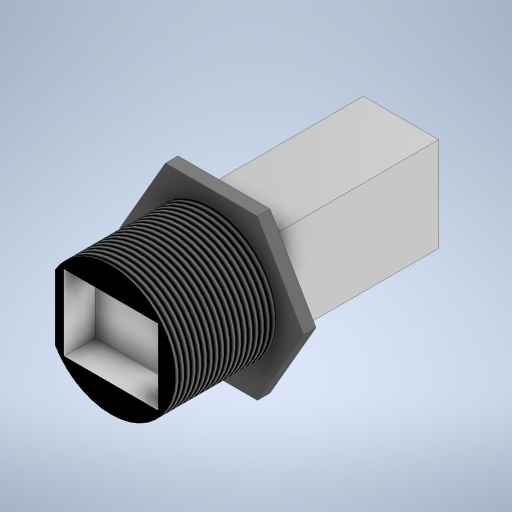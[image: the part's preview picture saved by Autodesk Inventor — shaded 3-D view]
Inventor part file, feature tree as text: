
AUTODESK INVENTOR PART (.ipt)
format: ipt  version: 2023 (Build 270158000, 158)  size: 297,472 bytes
history: native  units: in
note: dims shown in document units (in); Inventor stores cm internally (conversion verified against a paired STEP export)
features: extrude x4, sketch x4, thread x1
ambient origin geometry x8: Origin, YZ Plane, XZ Plane, XY Plane, X Axis, Y Axis, Z Axis, Center Point
bodies: Solid1 (feature_tree)
feature tree (9):
  extrude  "Extrusion1"  Depth=0.6299in TaperAngle=0.0deg
  extrude  "Extrusion2"  Depth=0.0787in TaperAngle=0.0deg
  extrude  "Extrusion3"  Depth=0.4724in
  thread  "Thread1"  [1 undecoded]
  extrude  "Extrusion4"  Depth=0.6299in TaperAngle=0.0deg
  sketch  "Sketch1"  dims[d0=0.8125in d1=0.6299in d2=0.0in]
  sketch  "Sketch2"  dims[d3=1.0in d4=0.0787in d5=0.0in]
  sketch  "Sketch3"  dims[d6=0.5906in d7=0.4724in d8=1.1102in d9=0.0in]
  sketch  "Sketch4"  dims[d10=0.7559in d11=0.6299in d12=0.0in d13=0.5906in d14=0.4724in d15=0.1969in d16=0.0in]
note: 1 required parameter value undecoded (feature->parameter linkage not recoverable at this tier; creation-order binding heuristic only, values carry confidence <= 0.55)
